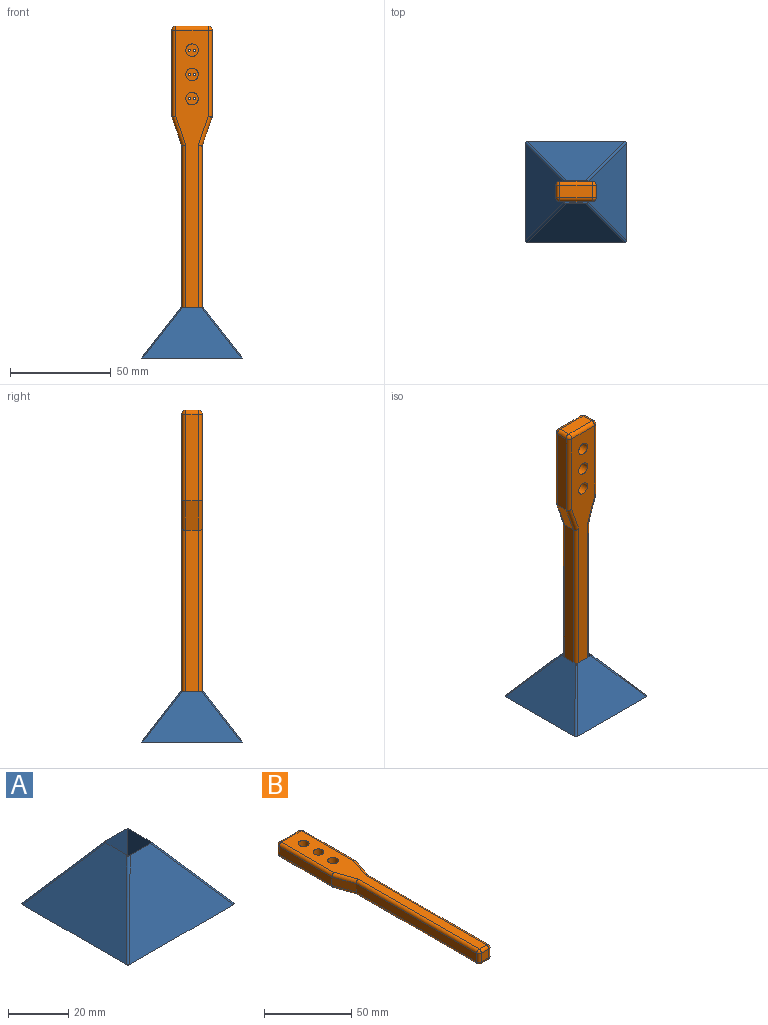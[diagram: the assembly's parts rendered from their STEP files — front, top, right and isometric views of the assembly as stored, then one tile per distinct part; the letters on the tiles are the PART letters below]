
ASSEMBLY  parts=2 mates=1
PART A: 14 faces, bbox 50.2x50.2x25.3 mm
  f0: plane 50x50mm, normal (0,0,-1), area 2499.5mm2, adj f1,f2,f3,f4,f10,f11,f12,f13
  f1: plane 48.42x25mm, normal (0,0.79,0.61), area 913.8mm2, adj f0,f6,f12,f13
  f2: plane 48.42x25mm, normal (-0.79,0,0.62), area 922.5mm2, adj f0,f7,f11,f12
  f3: plane 48.42x25mm, normal (0,-0.79,0.61), area 913.8mm2, adj f0,f8,f10,f11
  f4: plane 48.42x25mm, normal (0.79,0,0.62), area 922.5mm2, adj f0,f5,f10,f13
  f5: plane 20x11.35mm, normal (-1,0,0), area 226.8mm2, adj f4,f6,f8,f9,f10,f13
  f6: plane 20x11mm, normal (0,-1,0), area 219.8mm2, adj f1,f5,f7,f9,f12,f13
  f7: plane 20x11.35mm, normal (1,0,0), area 226.8mm2, adj f2,f6,f8,f9,f11,f12
  f8: plane 20x11mm, normal (0,1,0), area 219.8mm2, adj f3,f5,f7,f9,f10,f11
  f9: plane 11.35x11mm, normal (0,0,1), area 124.8mm2, adj f5,f6,f7,f8
  f10: cylinder r=1mm len=25.26mm, axis (-0.53,0.52,0.67), area 43.8mm2, adj f0,f3,f4,f5,f8
  f11: cylinder r=1mm len=25.26mm, axis (-0.53,-0.52,-0.67), area 43.8mm2, adj f0,f2,f3,f7,f8
  f12: cylinder r=1mm len=25.26mm, axis (0.53,-0.52,0.67), area 43.8mm2, adj f0,f1,f2,f6,f7
  f13: cylinder r=1mm len=25.26mm, axis (0.53,0.52,-0.67), area 43.8mm2, adj f0,f1,f4,f5,f6
PART B: 53 faces, bbox 20x159.6x10 mm
  f0: plane 43x6mm, normal (-1,0,0), area 258mm2, adj f1,f32,f37,f41
  f1: plane 14.55x6mm, normal (-0.95,-0.32,0), area 92.3mm2, adj f0,f2,f42,f45
  f2: plane 98x6mm, normal (-1,0,0), area 588mm2, adj f1,f46,f49,f52
  f3: plane 6x6mm, normal (0,-1,0), area 36mm2, adj f39,f47,f48,f52
  f4: plane 98x6mm, normal (1,0,0), area 588mm2, adj f5,f38,f39,f40
  f5: plane 14.24x6mm, normal (0.95,-0.32,0), area 90.3mm2, adj f4,f25,f34,f35
  f6: plane 42.67x6mm, normal (1,0,0), area 256mm2, adj f22,f24,f25,f26
  f7: cylinder r=3.1mm len=7mm, axis (0,0,-1), area 136.3mm2, adj f11,f18
  f8: cylinder r=3.1mm len=7mm, axis (0,0,-1), area 136.3mm2, adj f11,f15
  f9: plane 16x6mm, normal (0,1,0), area 96mm2, adj f22,f28,f31,f32
  f10: cylinder r=3.1mm len=7mm, axis (0,0,-1), area 136.3mm2, adj f11,f21
  f11: plane 155.55x16mm, normal (0,0,1), area 1342.2mm2, adj f7,f8,f10,f24,f28,f34,f37,f38
  f12: plane 155.55x16mm, normal (0,0,-1), area 1428mm2, adj f13,f14,f16,f17,f19,f20,f26,f31
  f13: cylinder r=0.5mm len=3mm, axis (0,0,-1), area 9.4mm2, adj f12,f15
  f14: cylinder r=0.5mm len=3mm, axis (0,0,-1), area 9.4mm2, adj f12,f15
  f15: plane 6.2x6.2mm, normal (0,0,1), area 28.6mm2, adj f8,f13,f14
  f16: cylinder r=0.5mm len=3mm, axis (0,0,-1), area 9.4mm2, adj f12,f18
  f17: cylinder r=0.5mm len=3mm, axis (0,0,-1), area 9.4mm2, adj f12,f18
  f18: plane 6.2x6.2mm, normal (0,0,1), area 28.6mm2, adj f7,f16,f17
  f19: cylinder r=0.5mm len=3mm, axis (0,0,-1), area 9.4mm2, adj f12,f21
  f20: cylinder r=0.5mm len=3mm, axis (0,0,-1), area 9.4mm2, adj f12,f21
  f21: plane 6.2x6.2mm, normal (0,0,1), area 28.6mm2, adj f10,f19,f20
  f22: cylinder r=2mm len=6mm, axis (0,0,-1), area 18.8mm2, adj f6,f9,f23,f27
  f23: sphere r=2mm, area 6.3mm2, adj f22,f24,f28
  f24: cylinder r=2mm len=42.67mm, axis (0,-1,0), area 134mm2, adj f6,f11,f23,f29
  f25: cylinder r=2mm len=6mm, axis (0,0,-1), area 4mm2, adj f5,f6,f29,f30
  f26: cylinder r=2mm len=42.67mm, axis (0,1,0), area 134mm2, adj f6,f12,f27,f30
  f27: sphere r=2mm, area 6.3mm2, adj f22,f26,f31
  f28: cylinder r=2mm len=16mm, axis (1,0,0), area 50.3mm2, adj f9,f11,f23,f33
  f29: sphere r=2mm, area 1.3mm2, adj f24,f25,f34
  f30: sphere r=2mm, area 1.3mm2, adj f25,f26,f35
  f31: cylinder r=2mm len=16mm, axis (-1,0,0), area 50.3mm2, adj f9,f12,f27,f36
  f32: cylinder r=2mm len=6mm, axis (0,0,-1), area 18.8mm2, adj f0,f9,f33,f36
  f33: sphere r=2mm, area 6.3mm2, adj f28,f32,f37
  f34: cylinder r=2mm len=15.2mm, axis (-0.32,-0.95,0), area 47.7mm2, adj f5,f11,f29,f38
  f35: cylinder r=2mm len=15.2mm, axis (0.32,0.95,0), area 47.7mm2, adj f5,f12,f30,f40
  f36: sphere r=2mm, area 6.3mm2, adj f31,f32,f41
  f37: cylinder r=2mm len=43mm, axis (0,1,0), area 134.7mm2, adj f0,f11,f33,f42
  f38: cylinder r=2mm len=98.33mm, axis (0,-1,0), area 308.3mm2, adj f4,f11,f34,f43
  f39: cylinder r=2mm len=6mm, axis (0,0,-1), area 18.8mm2, adj f3,f4,f43,f44
  f40: cylinder r=2mm len=98.33mm, axis (0,1,0), area 308.3mm2, adj f4,f12,f35,f44
  f41: cylinder r=2mm len=43mm, axis (0,-1,0), area 134.7mm2, adj f0,f12,f36,f45
  f42: cylinder r=2mm len=15.52mm, axis (-0.32,0.95,0), area 48.3mm2, adj f1,f11,f37,f46
  f43: sphere r=2mm, area 6.3mm2, adj f38,f39,f47
  f44: sphere r=2mm, area 6.3mm2, adj f39,f40,f48
  f45: cylinder r=2mm len=15.52mm, axis (0.32,-0.95,0), area 48.3mm2, adj f1,f12,f41,f49
  f46: cylinder r=2mm len=98.33mm, axis (0,1,0), area 308.3mm2, adj f2,f11,f42,f50
  f47: cylinder r=2mm len=6mm, axis (-1,0,0), area 18.8mm2, adj f3,f11,f43,f50
  f48: cylinder r=2mm len=6mm, axis (1,0,0), area 18.8mm2, adj f3,f12,f44,f51
  f49: cylinder r=2mm len=98.33mm, axis (0,-1,0), area 308.3mm2, adj f2,f12,f45,f51
  f50: sphere r=2mm, area 6.3mm2, adj f46,f47,f52
  f51: sphere r=2mm, area 6.3mm2, adj f48,f49,f52
  f52: cylinder r=2mm len=6mm, axis (0,0,-1), area 18.8mm2, adj f2,f3,f50,f51
PLACE A t=(26.38,0.29,-23.83)mm
PLACE B rot(axis=(1,0,0),90deg) t=(39.7,5.29,59.09)mm
MATE fastened B.f3 <-> A.f9  axis (0,0,-1) through (26.38,0.29,-18.83)mm
